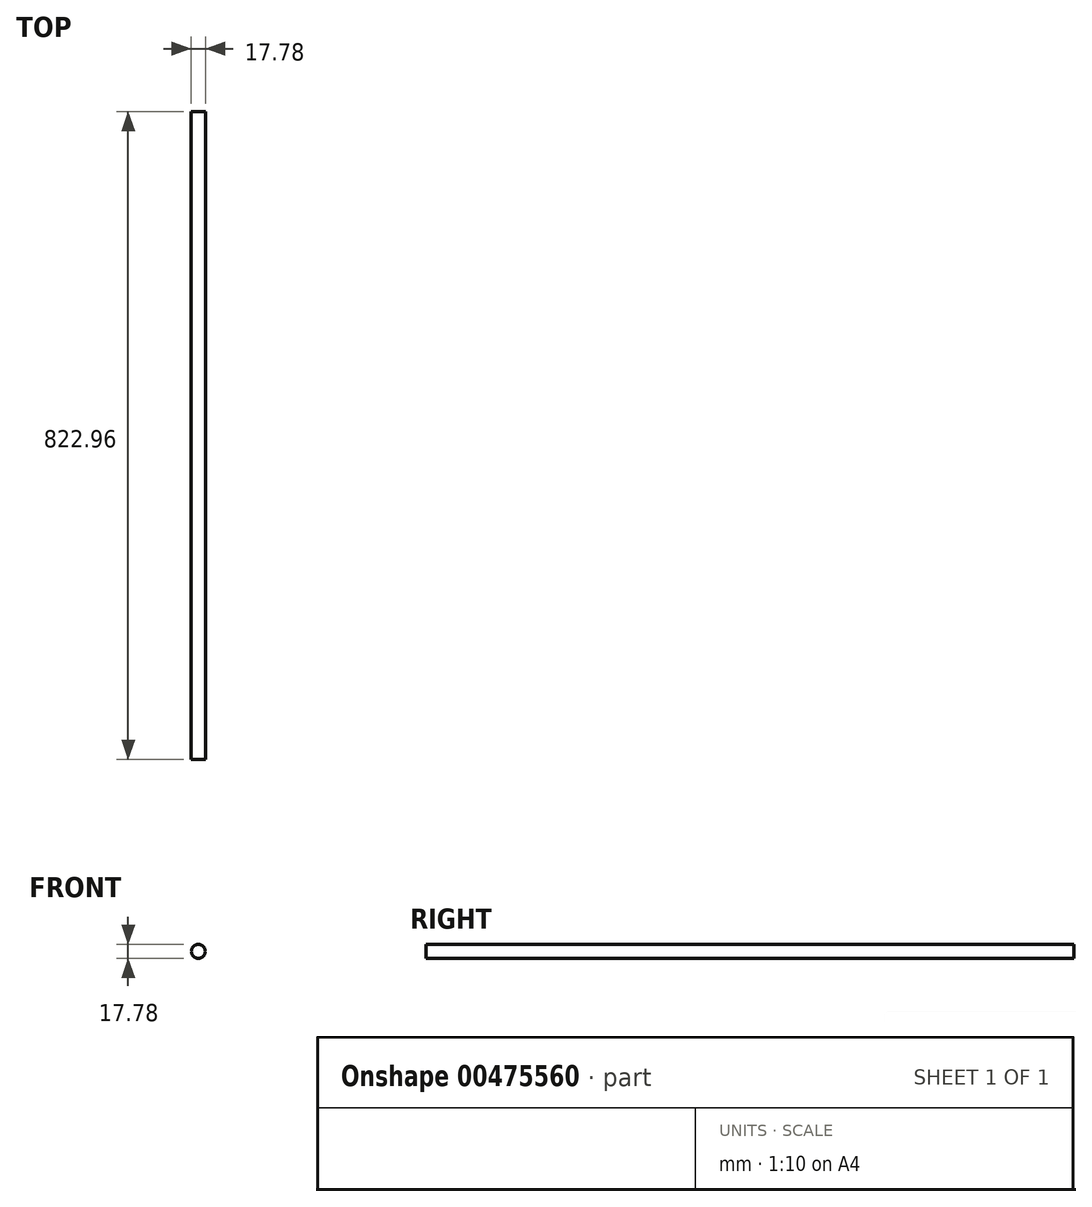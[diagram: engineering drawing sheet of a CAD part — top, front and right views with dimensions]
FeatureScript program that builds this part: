
annotation { "Feature Type Name" : "Feature", "Feature Type Description" : "" }
export const myFeature = defineFeature(function(context is Context, id is Id, definition is map)
    precondition{}
    {
        {
            var Q0;
            Q0=qCreatedBy(makeId("Front.planeOp"),FACE);
            var sketch = newSketch(context, id + "F0", { "sketchPlane" : qUnion([Q0])});
            skCircle(sketch, "E0", {"center": v(-86.26, 6.9) * mm, "radius": 8.9 * mm});
            skSolve(sketch);
        }
        {
            var Q0;
            Q0 = qSketchRegion(id + "F0", true);
            extrude(context, id + "F1", {"entities" : qUnion([Q0]), "depth" : 822.96 * mm});
        }
    });
